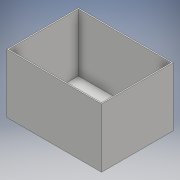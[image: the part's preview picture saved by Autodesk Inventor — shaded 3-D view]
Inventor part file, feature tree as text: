
AUTODESK INVENTOR PART (.ipt)
format: ipt  version: 2018 (Build 220112000, 112)  size: 104,448 bytes
history: native  units: mm
features: sketch x3, hole x2, extrude x1, shell x1
ambient origin geometry x8: Origin, YZ Plane, XZ Plane, XY Plane, X Axis, Y Axis, Z Axis, Center Point
bodies: Solid1 (feature_tree)
feature tree (7):
  extrude  "Extrusion1"  Depth=60.0mm
  shell  "Shell1"  Thickness=50.0mm
  hole  "Hole1"  [1 undecoded]
  hole  "Hole2"  [1 undecoded]
  sketch  "Sketch1"  dims[d2=80.0mm d3=60.0mm d4=50.0mm d5=0.0mm]
  sketch  "Sketch2"  dims[d6=1.0mm d7=2.0mm]
  sketch  "Sketch3"  dims[d8=2.0mm d9=6.0mm d10=4.0mm d11=2.0mm d12=90.0deg d13=51.0mm d14=0.0mm d15=2.0mm d16=2.0mm d17=6.0mm d18=4.0mm d19=2.0mm d20=90.0deg d21=51.0mm d22=0.0mm]
note: 2 required parameter values undecoded (feature->parameter linkage not recoverable at this tier; creation-order binding heuristic only, values carry confidence <= 0.55)
